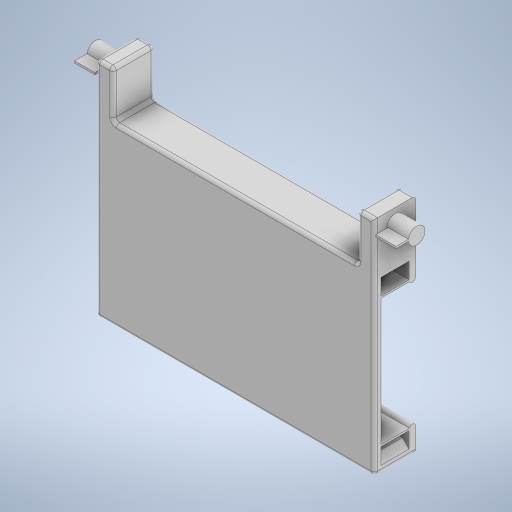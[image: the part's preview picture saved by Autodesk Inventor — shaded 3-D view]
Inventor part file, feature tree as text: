
AUTODESK INVENTOR PART (.ipt)
format: ipt  version: 2024 (Build 280153000, 153)  size: 423,936 bytes
history: native  units: mm
features: extrude x8, sketch x8, fillet x6, mirror x4, chamfer x1
ambient origin geometry x8: Origin, YZ Plane, XZ Plane, XY Plane, X Axis, Y Axis, Z Axis, Center Point
bodies: Volumenkörper1 (feature_tree)
feature tree (27):
  extrude  "Extrusion1"  Depth=5.2mm TaperAngle=0.0deg
  extrude  "Extrusion2"  Depth=39.7mm
  extrude  "Extrusion3"  Depth=1.0mm
  extrude  "Extrusion7"  Depth=2.0mm
  mirror  "Spiegeln2"
  extrude  "Extrusion8"  Depth=2.0mm
  extrude  "Extrusion9"  Depth=1.5mm
  mirror  "Spiegeln3"
  extrude  "Extrusion10"  Depth=0.3mm
  mirror  "Spiegeln4"
  extrude  "Extrusion11"  Depth=0.25mm TaperAngle=0.0deg
  mirror  "Spiegeln5"
  fillet  "Rundung1"  Radius=2.0mm
  fillet  "Rundung2"  Radius=2.5mm
  fillet  "Rundung3"  Radius=3.25mm
  fillet  "Rundung4"  Radius=0.3mm
  chamfer  "Fasen1"  Distance=0.4mm
  fillet  "Rundung5"  Radius=10.0mm
  fillet  "Rundung6"  Radius=0.3mm
  sketch  "Skizze1"  dims[d2=1.0mm d3=0.0mm d6=5.2mm d7=0.0mm]
  sketch  "Skizze2"  dims[d11=1.0mm d12=0.0mm d24=39.7mm]
  sketch  "Skizze3"  dims[d25=22.4mm d26=1.0mm]
  sketch  "Skizze7"  dims[d27=0.0mm d30=2.0mm]
  sketch  "Skizze8"  dims[d31=2.0mm d35=2.0mm]
  sketch  "Skizze9"  dims[d36=2.0mm d38=1.5mm]
  sketch  "Skizze11"  dims[d39=2.5mm d40=0.3mm d41=-8.726646mm]
  sketch  "Skizze12"  dims[d42=2.5mm d43=7.0mm d44=0.0mm d45=2.0mm d46=2.5mm d47=3.25mm d48=0.0mm d50=0.3mm d51=0.4mm d52=10.0mm d53=0.0mm d54=0.3mm d55=0.15mm d56=0.15mm d57=0.2mm d58=0.0mm d59=0.0mm d60=0.5mm d61=0.5mm d62=0.5mm d63=0.5mm d64=1.0mm d65=2.0mm d66=45.0deg d67=0.5mm d68=0.25mm d69=0.0mm d70=0.0mm d71=0.0mm]
